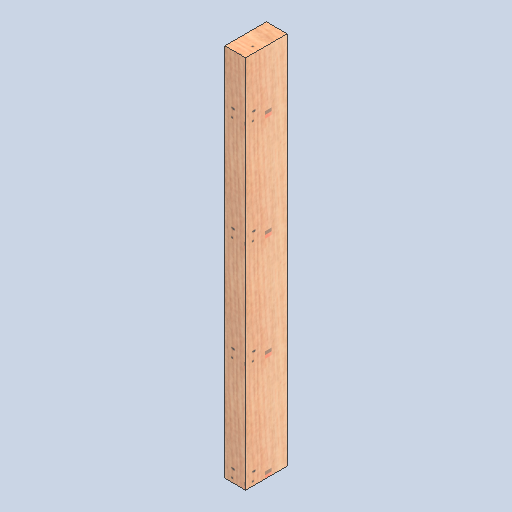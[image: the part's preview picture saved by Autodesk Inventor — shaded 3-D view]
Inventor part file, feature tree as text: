
AUTODESK INVENTOR PART (.ipt)
format: ipt  version: 2025 (Build 290162000, 162)  size: 331,264 bytes
history: native  units: in
note: dims shown in document units (in); Inventor stores cm internally (conversion verified against a paired STEP export)
features: extrude x1, sketch x1
ambient origin geometry x8: Origin, YZ Plane, XZ Plane, XY Plane, X Axis, Y Axis, Z Axis, Center Point
bodies: Solid1 (feature_tree)
feature tree (2):
  extrude  "Extrusion1"  Depth=4.0in
  sketch  "Sketch1"  dims[d0=2.0in d1=4.0in d2=36.0in d3=0.0in]
